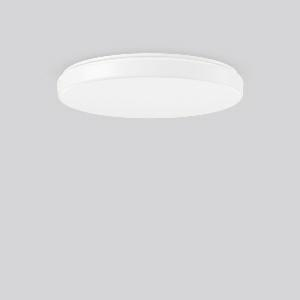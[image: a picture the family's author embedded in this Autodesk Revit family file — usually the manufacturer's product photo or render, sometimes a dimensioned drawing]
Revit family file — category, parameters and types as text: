
# Revit family: flat_polymero_kreis_slim_312087_002_3_76_4a2b
name_source: partatom
category: Lighting Fixtures
units: mm (PartAtom-declared; Revit-internal decimal feet)

## family parameters
Cut with Voids When Loaded = No
Host = Face
Light Source = No
Part Type = Normal
Room Calculation Point = No
Round Connector Dimension = Use Diameter
Shared = No

## types (1)
- FLAT POLYMERO KREIS SLIM (1 x LED Modul 840, 3700 lm, 4000)
    Apparent Load = 38 VA
    CIE Flux Codes = 42 72 91 82 100
    Color Rendering = 80
    Color Temperature = 4000
    Default Elevation = 1800 mm
    Description = Series: FLAT POLYMERO KREIS SLIM
Flat decorative round LED surface-mounted luminaire. Base: metal, powder-coated. Diffuser made of non-yellowing plastic (PMMA), opal. Diffuser fastening: patented push system. Suitable for Ceiling mounting, Wall (surface). 
Colour: white
Diameter: 515 mm
Height: 70 mm
Lamp: LED
Socket: without socket
Colour temperature: 4000K
Colour rendering index (CRI): 83
System power: 38 W
Rated luminous flux: 3700 lm
Luminous efficiency: 97 lm/W
Control gear: AC power, DALI dimmable
Protection class: I
Type of protection: IP 40
    Height = 70 mm
    Lamp = 1 x LED Modul 840
    Lamp Light Flux = 3700 lm
    Lamp count = 1
    Length = 515 mm
    Lifetime = 50000 h
    Luminous efficacy = 97 lm/W
    Manufacturer = RZB
    ModVariant = No
    Model = 312087.002.3.76
    Mounting Place = Ceiling, Wall
    Mounting Type = Surface mounted
    Number of Poles = 1
    OnlyDefault = Yes
    Power Factor = 1
    Product Name = FLAT POLYMERO KREIS SLIM
    Product group = Surface mounted ceiling and wall luminaires
    ProductGroupID = 305
    Protection Class = Protection class I
    Protection Degree = IP 40
    RLX_Detail_Level = 1
    RLX_Emergency_Light_Flux = 0 lm
    RLX_Emergency_Type = 0
    RLX_Emergency_Type_DB = No
    RlxData = <blob elided: 42961 chars, md5=9bdf97ba>
    Socket = socket
    Standby Power = 0 W
    System Light Flux = 3700 lm
    System Power = 38 W
    Type Comments = Product without accessories
    Type Image = 312087.002.jpg
    URL = http://relux.com
    VarID = ---
    Voltage = 230 V
    Voltage Range = 220-240 V
    Weight = 0.00 kg
    Width = 0 mm  [stored 0 ft]

note: [stored X ft] marks values corroborated as IEEE doubles in the binary element streams (Revit-internal decimal feet)

## geometry (parser evidence)
native form markers: Blend x4, Sweep x12
no freeform markers — native parametric forms only
